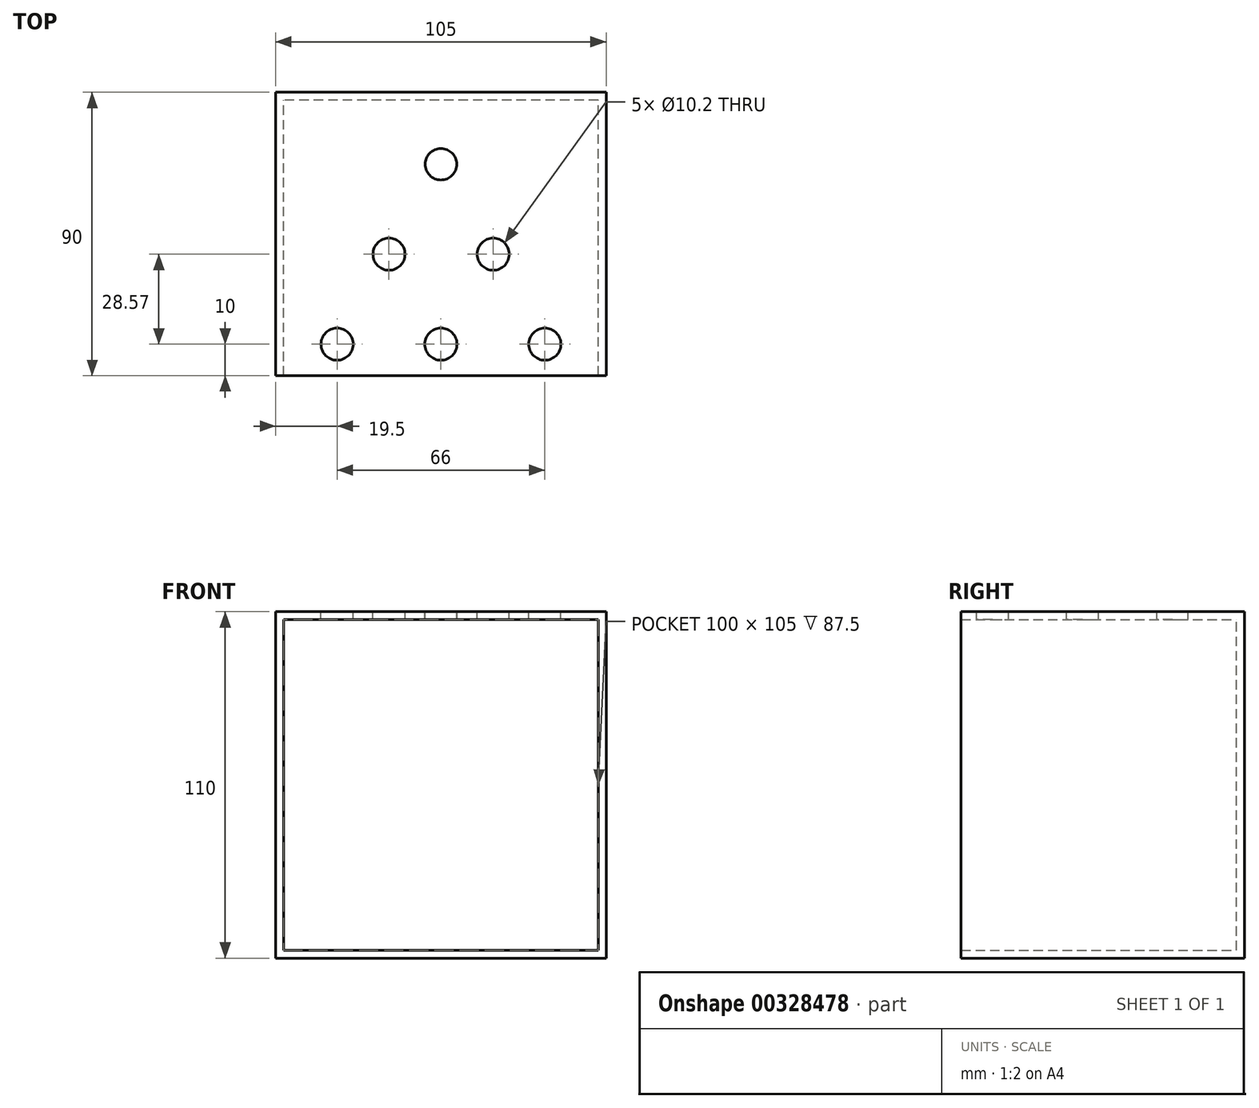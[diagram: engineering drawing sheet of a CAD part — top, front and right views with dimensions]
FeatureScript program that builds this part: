
annotation { "Feature Type Name" : "Feature", "Feature Type Description" : "" }
export const myFeature = defineFeature(function(context is Context, id is Id, definition is map)
    precondition{}
    {
        {
            var Q0;
            Q0=qCreatedBy(makeId("Front.planeOp"),FACE);
            var sketch = newSketch(context, id + "F0", { "sketchPlane" : qUnion([Q0])});
            skLineSegment(sketch, "E0.bottom", {"start": v(52.5, -55) * mm, "end": v(-52.5, -55) * mm});
            skLineSegment(sketch, "E0.top", {"start": v(52.5, 55) * mm, "end": v(-52.5, 55) * mm});
            skLineSegment(sketch, "E0.left", {"start": v(52.5, -55) * mm, "end": v(52.5, 55) * mm});
            skLineSegment(sketch, "E0.right", {"start": v(-52.5, -55) * mm, "end": v(-52.5, 55) * mm});
            skPoint(sketch, "E0.middle", {"position": v(0, 0) * mm});
            skSolve(sketch);
        }
        {
            var Q0;
            Q0 = qSketchRegion(id + "F0", true);
            extrude(context, id + "F1", {"entities" : qUnion([Q0]), "depth" : 90 * mm});
        }
        {
            var Q0;
            Q0=makeQuery(id+"F1.opExtrude","CAP_FACE",FACE,{"disambiguationData":[OSD([sQuery(id+"F0.wireOp",EDGE,"E0.bottom"),sQuery(id+"F0.wireOp",EDGE,"E0.top"),sQuery(id+"F0.wireOp",EDGE,"E0.left"),sQuery(id+"F0.wireOp",EDGE,"E0.right")])],"isStart":false});
            shell(context, id + "F2", {"entities" : qUnion([Q0]), "thickness" : 2.5 * mm});
        }
        {
            var Q0;
            Q0=makeQuery(id+"F1.opExtrude","SWEPT_FACE",FACE,{"disambiguationData":[OSD([sQuery(id+"F0.wireOp",EDGE,"E0.top")])]});
            var sketch = newSketch(context, id + "F3", { "sketchPlane" : qUnion([Q0])});
            skLineSegment(sketch, "E1", {"start": v(-52.5, -80) * mm, "end": v(52.5, -80) * mm, "construction": true});
            skPoint(sketch, "E2", {"position": v(0, -80) * mm});
            skPoint(sketch, "E3", {"position": v(33, -80) * mm});
            skPoint(sketch, "E4", {"position": v(-33, -80) * mm});
            skCircle(sketch, "E5", {"center": v(-33, -80) * mm, "radius": 5.1 * mm});
            skCircle(sketch, "E6", {"center": v(0, -80) * mm, "radius": 5.1 * mm});
            skCircle(sketch, "E7", {"center": v(33, -80) * mm, "radius": 5.1 * mm});
            skLineSegment(sketch, "E8", {"start": v(-33, -80) * mm, "end": v(-16.5, -80) * mm, "construction": true});
            skLineSegment(sketch, "E9", {"start": v(-16.5, -80) * mm, "end": v(-16.5, 0) * mm, "construction": true});
            skPoint(sketch, "E10", {"position": v(-16.5, -51.43) * mm});
            skLineSegment(sketch, "E11", {"start": v(0, -80) * mm, "end": v(16.6, -80) * mm, "construction": true});
            skLineSegment(sketch, "E12", {"start": v(16.6, -80) * mm, "end": v(16.6, 0) * mm, "construction": true});
            skPoint(sketch, "E13", {"position": v(16.6, -51.43) * mm});
            skCircle(sketch, "E14", {"center": v(16.6, -51.43) * mm, "radius": 5.1 * mm});
            skCircle(sketch, "E15", {"center": v(-16.5, -51.43) * mm, "radius": 5.1 * mm});
            skCircle(sketch, "E16", {"center": v(0, -22.86) * mm, "radius": 5 * mm});
            skSolve(sketch);
        }
        {
            var Q0;
            Q0=makeQuery(id+"F3.imprint","IMPRINT",FACE,{"disambiguationData":[TD([[makeQuery(id+"F3.imprint","IMPRINT",EDGE,{"derivedFrom":sQuery(id+"F3.wireOp",EDGE,"E14")}),1.0]])]});
            var Q1;
            Q1=makeQuery(id+"F3.imprint","IMPRINT",FACE,{"disambiguationData":[TD([[makeQuery(id+"F3.imprint","IMPRINT",EDGE,{"derivedFrom":sQuery(id+"F3.wireOp",EDGE,"E7")}),1.0]])]});
            var Q2;
            Q2=makeQuery(id+"F3.imprint","IMPRINT",FACE,{"disambiguationData":[TD([[makeQuery(id+"F3.imprint","IMPRINT",EDGE,{"derivedFrom":sQuery(id+"F3.wireOp",EDGE,"E6")}),1.0]])]});
            var Q3;
            Q3=makeQuery(id+"F3.imprint","IMPRINT",FACE,{"disambiguationData":[TD([[makeQuery(id+"F3.imprint","IMPRINT",EDGE,{"derivedFrom":sQuery(id+"F3.wireOp",EDGE,"E5")}),1.0]])]});
            var Q4;
            Q4=makeQuery(id+"F3.imprint","IMPRINT",FACE,{"disambiguationData":[TD([[makeQuery(id+"F3.imprint","IMPRINT",EDGE,{"derivedFrom":sQuery(id+"F3.wireOp",EDGE,"E15")}),1.0]])]});
            var Q5;
            Q5=makeQuery(id+"F3.imprint","IMPRINT",FACE,{"disambiguationData":[TD([[makeQuery(id+"F3.imprint","IMPRINT",EDGE,{"derivedFrom":sQuery(id+"F3.wireOp",EDGE,"E16")}),1.0]])]});
            extrude(context, id + "F4", {"entities" : qUnion([Q0, Q1, Q2, Q3, Q4, Q5]), "operationType" : NewBodyOperationType.REMOVE, "oppositeDirection" : true, "depth" : 25 * mm});
        }
    });
